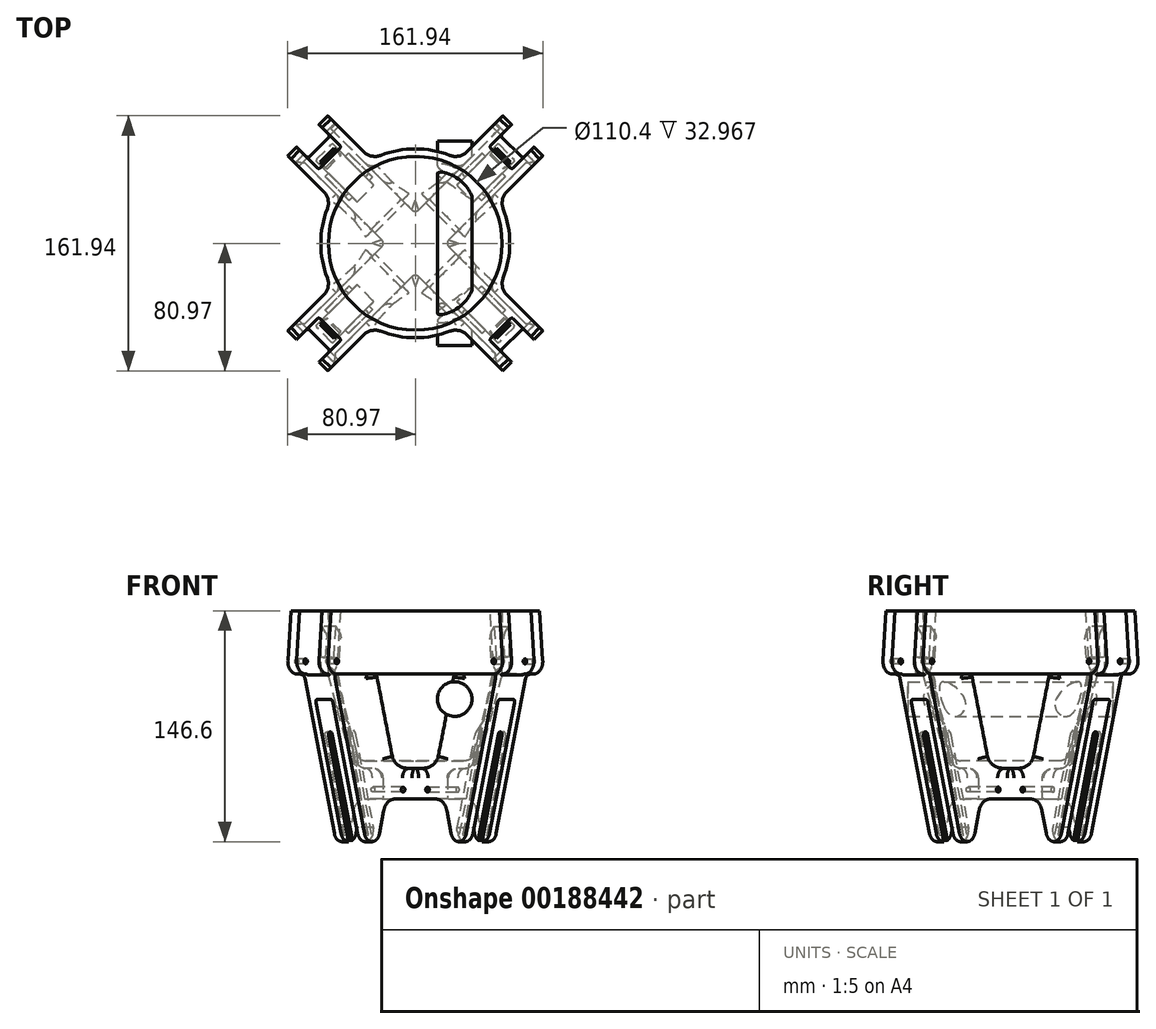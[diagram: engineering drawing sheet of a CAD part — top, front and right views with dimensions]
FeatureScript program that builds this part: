
annotation { "Feature Type Name" : "Feature", "Feature Type Description" : "" }
export const myFeature = defineFeature(function(context is Context, id is Id, definition is map)
    precondition{}
    {
        {
            var Q0;
            Q0=qCreatedBy(makeId("Top.planeOp"),FACE);
            var sketch = newSketch(context, id + "F0", { "sketchPlane" : qUnion([Q0])});
            skCircle(sketch, "E0", {"center": v(0, 0) * mm, "radius": 230 * mm, "construction": true});
            skLineSegment(sketch, "E1", {"start": v(-162.63, 162.63) * mm, "end": v(162.63, -162.63) * mm, "construction": true});
            skLineSegment(sketch, "E2", {"start": v(-162.63, -162.63) * mm, "end": v(162.63, 162.63) * mm, "construction": true});
            skLineSegment(sketch, "E3", {"start": v(0, 230) * mm, "end": v(0, -230) * mm, "construction": true});
            skCircle(sketch, "E4", {"center": v(-162.63, 162.63) * mm, "radius": 139.7 * mm, "construction": true});
            skCircle(sketch, "E5", {"center": v(162.63, 162.63) * mm, "radius": 139.7 * mm, "construction": true});
            skCircle(sketch, "E6", {"center": v(162.63, -162.63) * mm, "radius": 139.7 * mm, "construction": true});
            skCircle(sketch, "E7", {"center": v(-162.63, -162.63) * mm, "radius": 139.7 * mm, "construction": true});
            skCircle(sketch, "E8", {"center": v(0, 0) * mm, "radius": 80 * mm, "construction": true});
            skSolve(sketch);
        }
        {
            var Q0;
            Q0=sQuery(id+"F0.wireOp",EDGE,"E2");
            cPlane(context, id + "F1", {"entities" : qUnion([Q0]), "cplaneType" : CPlaneType.LINE_ANGLE, "offset" : 25 * mm, "angle" : 90 * degree, "width" : 150 * mm, "height" : 150 * mm});
        }
        {
            var Q0;
            Q0=qCreatedBy(id+"F1.planeOp",FACE);
            var sketch = newSketch(context, id + "F2", { "sketchPlane" : qUnion([Q0])});
            skLineSegment(sketch, "E9", {"start": v(0, 304.8) * mm, "end": v(0, -303.3) * mm, "construction": true});
            skLineSegment(sketch, "E10", {"start": v(0, 0) * mm, "end": v(244.07, 21.35) * mm, "construction": true});
            skLineSegment(sketch, "E11.0", {"start": v(80, 304.8) * mm, "end": v(80, -303.3) * mm, "construction": true});
            skLineSegment(sketch, "E12", {"start": v(244.07, 21.35) * mm, "end": v(243.52, 27.58) * mm});
            skLineSegment(sketch, "E13", {"start": v(243.52, 27.58) * mm, "end": v(74.17, 12.76) * mm});
            skLineSegment(sketch, "E14", {"start": v(74.17, 12.76) * mm, "end": v(74.71, 6.54) * mm});
            skLineSegment(sketch, "E15.MirrorCS", {"start": v(244.07, 21.35) * mm, "end": v(244.61, 15.13) * mm});
            skLineSegment(sketch, "E16.MirrorCS", {"start": v(75.26, 0.31) * mm, "end": v(74.71, 6.54) * mm});
            skLineSegment(sketch, "E17.MirrorCS", {"start": v(244.61, 15.13) * mm, "end": v(75.26, 0.31) * mm});
            skLineSegment(sketch, "E18", {"start": v(77.78, 28.89) * mm, "end": v(80.55, -2.74) * mm});
            skLineSegment(sketch, "E19", {"start": v(77.78, 28.89) * mm, "end": v(89.73, 29.93) * mm});
            skLineSegment(sketch, "E20", {"start": v(89.73, 29.93) * mm, "end": v(93.9, 18.5) * mm});
            skLineSegment(sketch, "E21", {"start": v(93.9, 18.5) * mm, "end": v(128.61, 21.54) * mm});
            skLineSegment(sketch, "E22", {"start": v(128.61, 21.54) * mm, "end": v(130.36, 1.62) * mm});
            skLineSegment(sketch, "E23", {"start": v(130.36, 1.62) * mm, "end": v(96.48, -1.35) * mm});
            skArc(sketch, "E24", {"start": v(80.55, -2.74) * mm, "mid": v(89.21, -10.01) * mm, "end": v(96.48, -1.35) * mm});
            skCircle(sketch, "E25", {"center": v(122.53, 10.72) * mm, "radius": 1.59 * mm});
            skLineSegment(sketch, "E26", {"start": v(88.51, -2.04) * mm, "end": v(87.67, 7.67) * mm, "construction": true});
            skLineSegment(sketch, "E27", {"start": v(88.51, -2.04) * mm, "end": v(88.51, -82.67) * mm, "construction": true});
            skCircle(sketch, "E28", {"center": v(88.51, -2.04) * mm, "radius": 157.3 * mm, "construction": true});
            skLineSegment(sketch, "E29", {"start": v(88.51, -2.04) * mm, "end": v(47.8, -153.99) * mm, "construction": true});
            skLineSegment(sketch, "E30.0", {"start": v(81.75, -0.23) * mm, "end": v(42.92, -145.15) * mm, "construction": true});
            skCircle(sketch, "E31", {"center": v(88.51, -2.04) * mm, "radius": 36.33 * mm, "construction": true});
            skLineSegment(sketch, "E32.0", {"start": v(98.01, -4.27) * mm, "end": v(57.3, -156.22) * mm, "construction": true});
            skPoint(sketch, "E33", {"position": v(88.87, -38.37) * mm});
            skCircle(sketch, "E34", {"center": v(88.87, -38.37) * mm, "radius": 1.59 * mm});
            skCircle(sketch, "E35", {"center": v(122.53, 10.72) * mm, "radius": 80 * mm, "construction": true});
            skLineSegment(sketch, "E36", {"start": v(122.53, 10.72) * mm, "end": v(68.8, -48.55) * mm, "construction": true});
            skArc(sketch, "E37.0.startCap", {"start": v(118.83, 14.08) * mm, "mid": v(125.89, 14.42) * mm, "end": v(126.24, 7.36) * mm});
            skArc(sketch, "E37.0.endCap", {"start": v(72.51, -51.91) * mm, "mid": v(65.45, -52.26) * mm, "end": v(65.1, -45.2) * mm});
            skLineSegment(sketch, "E37.0.left", {"start": v(126.24, 7.36) * mm, "end": v(72.51, -51.91) * mm});
            skLineSegment(sketch, "E37.0.right", {"start": v(118.83, 14.08) * mm, "end": v(65.1, -45.2) * mm});
            skCircle(sketch, "E38", {"center": v(88.51, -2.04) * mm, "radius": 1.59 * mm});
            skCircle(sketch, "E39", {"center": v(68.8, -48.55) * mm, "radius": 1.59 * mm});
            skCircle(sketch, "E40", {"center": v(88.87, -38.37) * mm, "radius": 80 * mm, "construction": true});
            skPoint(sketch, "E41", {"position": v(52.45, -109.6) * mm});
            skLineSegment(sketch, "E42", {"start": v(68.8, -48.55) * mm, "end": v(139.52, -119.26) * mm, "construction": true});
            skLineSegment(sketch, "E43", {"start": v(148.5, -119.26) * mm, "end": v(130.54, -119.26) * mm});
            skLineSegment(sketch, "E44", {"start": v(130.54, -119.26) * mm, "end": v(59.83, -48.55) * mm});
            skLineSegment(sketch, "E45", {"start": v(59.83, -48.55) * mm, "end": v(68.8, -39.57) * mm});
            skLineSegment(sketch, "E46", {"start": v(68.8, -39.57) * mm, "end": v(148.5, -119.26) * mm});
            skCircle(sketch, "E47", {"center": v(68.8, -48.55) * mm, "radius": 100 * mm, "construction": true});
            skCircle(sketch, "E48", {"center": v(122.69, -102.44) * mm, "radius": 1.59 * mm});
            skCircle(sketch, "E49", {"center": v(52.45, -109.6) * mm, "radius": 1.59 * mm});
            skLineSegment(sketch, "E50", {"start": v(52.45, -109.6) * mm, "end": v(26.57, -206.2) * mm, "construction": true});
            skLineSegment(sketch, "E51", {"start": v(22.08, -198.42) * mm, "end": v(47.96, -101.82) * mm});
            skLineSegment(sketch, "E52", {"start": v(47.96, -101.82) * mm, "end": v(60.23, -105.11) * mm});
            skCircle(sketch, "E53", {"center": v(32.73, -183.2) * mm, "radius": 1.59 * mm});
            skLineSegment(sketch, "E54", {"start": v(60.23, -105.11) * mm, "end": v(31.06, -213.97) * mm});
            skLineSegment(sketch, "E55", {"start": v(31.06, -213.97) * mm, "end": v(22.08, -198.42) * mm});
            skLineSegment(sketch, "E56", {"start": v(88.87, -38.37) * mm, "end": v(52.45, -109.6) * mm, "construction": true});
            skCircle(sketch, "E57", {"center": v(122.69, -102.44) * mm, "radius": 100 * mm, "construction": true});
            skCircle(sketch, "E58", {"center": v(32.73, -183.2) * mm, "radius": 100 * mm, "construction": true});
            skCircle(sketch, "E59", {"center": v(24.49, -83.54) * mm, "radius": 1.59 * mm});
            skLineSegment(sketch, "E60", {"start": v(24.49, -83.54) * mm, "end": v(122.69, -102.44) * mm, "construction": true});
            skArc(sketch, "E61.0.startCap", {"start": v(23.54, -88.45) * mm, "mid": v(19.58, -82.6) * mm, "end": v(25.43, -78.63) * mm});
            skArc(sketch, "E61.0.endCap", {"start": v(123.63, -97.53) * mm, "mid": v(127.6, -103.38) * mm, "end": v(121.74, -107.35) * mm});
            skLineSegment(sketch, "E61.0.left", {"start": v(25.43, -78.63) * mm, "end": v(123.63, -97.53) * mm});
            skLineSegment(sketch, "E61.0.right", {"start": v(23.54, -88.45) * mm, "end": v(121.74, -107.35) * mm});
            skLineSegment(sketch, "E62", {"start": v(24.49, -83.54) * mm, "end": v(32.73, -183.2) * mm, "construction": true});
            skArc(sketch, "E63.0.startCap", {"start": v(19.5, -83.96) * mm, "mid": v(24.08, -78.56) * mm, "end": v(29.47, -83.13) * mm});
            skArc(sketch, "E63.0.endCap", {"start": v(37.7, -182.8) * mm, "mid": v(33.14, -188.19) * mm, "end": v(27.74, -183.62) * mm});
            skLineSegment(sketch, "E63.0.left", {"start": v(29.47, -83.13) * mm, "end": v(37.7, -182.8) * mm});
            skLineSegment(sketch, "E63.0.right", {"start": v(19.5, -83.96) * mm, "end": v(27.74, -183.62) * mm});
            skCircle(sketch, "E64", {"center": v(88.51, -2.04) * mm, "radius": 32.74 * mm, "construction": true});
            skLineSegment(sketch, "E65", {"start": v(88.51, -2.04) * mm, "end": v(121.26, -2.04) * mm, "construction": true});
            skLineSegment(sketch, "E66.0", {"start": v(354.77, 67.43) * mm, "end": v(76.44, 43.08) * mm});
            skLineSegment(sketch, "E67", {"start": v(218.22, 25.37) * mm, "end": v(215.6, 55.25) * mm, "construction": true});
            skCircle(sketch, "E68", {"center": v(88.51, -2.04) * mm, "radius": 275.17 * mm, "construction": true});
            skLineSegment(sketch, "E69.0", {"start": v(135.04, -6.12) * mm, "end": v(62.73, -276) * mm});
            skLineSegment(sketch, "E70", {"start": v(89.73, 29.93) * mm, "end": v(0, 29.93) * mm, "construction": true});
            skSolve(sketch);
        }
        {
            var Q0;
            Q0=qCreatedBy(id+"F1.planeOp",FACE);
            var sketch = newSketch(context, id + "F3", { "sketchPlane" : qUnion([Q0])});
            skLineSegment(sketch, "E71", {"start": v(96.48, -1.35) * mm, "end": v(93.74, 30) * mm});
            skLineSegment(sketch, "E72", {"start": v(93.74, 30) * mm, "end": v(0, 30) * mm});
            skLineSegment(sketch, "E73", {"start": v(0, 30) * mm, "end": v(0, -89.54) * mm});
            skLineSegment(sketch, "E74", {"start": v(0, -89.54) * mm, "end": v(32.15, -89.54) * mm});
            skLineSegment(sketch, "E75", {"start": v(41.81, -96.96) * mm, "end": v(45.69, -111.41) * mm});
            skLineSegment(sketch, "E76", {"start": v(59.2, -111.41) * mm, "end": v(85.78, -12.27) * mm});
            skArc(sketch, "E77", {"start": v(88.63, -10.04) * mm, "mid": v(94.45, -7.4) * mm, "end": v(96.48, -1.35) * mm});
            skArc(sketch, "E78.filletArc", {"start": v(45.69, -111.41) * mm, "mid": v(52.45, -116.6) * mm, "end": v(59.2, -111.41) * mm});
            skPoint(sketch, "E79.visualSharp", {"position": v(39.83, -89.54) * mm});
            skArc(sketch, "E79.filletArc", {"start": v(41.81, -96.96) * mm, "mid": v(38.24, -91.61) * mm, "end": v(32.15, -89.54) * mm});
            skPoint(sketch, "E80.visualSharp", {"position": v(86.44, -9.77) * mm});
            skArc(sketch, "E80.filletArc", {"start": v(88.63, -10.04) * mm, "mid": v(86.83, -10.68) * mm, "end": v(85.78, -12.27) * mm});
            skPoint(sketch, "E81", {"position": v(24.49, -83.54) * mm});
            skSolve(sketch);
        }
        {
            var Q0;
            Q0 = qSketchRegion(id + "F3", true);
            extrude(context, id + "F4", {"entities" : qUnion([Q0]), "endBound" : BoundingType.SYMMETRIC, "depth" : 36 * mm, "offsetDistance" : 25 * mm});
        }
        {
            var Q0;
            Q0=qCreatedBy(id+"F1.planeOp",FACE);
            var sketch = newSketch(context, id + "F5", { "sketchPlane" : qUnion([Q0])});
            skLineSegment(sketch, "E82", {"start": v(76.68, 30) * mm, "end": v(79.55, -2.83) * mm});
            skLineSegment(sketch, "E83", {"start": v(76.68, 30) * mm, "end": v(94.75, 30) * mm});
            skLineSegment(sketch, "E84", {"start": v(94.75, 30) * mm, "end": v(98.34, -11.04) * mm});
            skLineSegment(sketch, "E85", {"start": v(98.34, -11.04) * mm, "end": v(88.51, -11.04) * mm});
            skArc(sketch, "E86", {"start": v(79.55, -2.83) * mm, "mid": v(82.43, -8.68) * mm, "end": v(88.51, -11.04) * mm});
            skSolve(sketch);
        }
        {
            var Q0;
            Q0 = qSketchRegion(id + "F5", true);
            extrude(context, id + "F6", {"entities" : qUnion([Q0]), "operationType" : NewBodyOperationType.REMOVE, "endBound" : BoundingType.SYMMETRIC, "oppositeDirection" : true, "depth" : 20 * mm, "offsetDistance" : 25 * mm});
        }
        {
            var Q0;
            Q0=makeQuery(id+"F4.opExtrude","SWEPT_FACE",FACE,{"disambiguationData":[OSD([sQuery(id+"F3.wireOp",EDGE,"E73")])]});
            var sketch = newSketch(context, id + "F7", { "sketchPlane" : qUnion([Q0])});
            skLineSegment(sketch, "E87", {"start": v(13.5, -119.35) * mm, "end": v(13.5, -10) * mm});
            skLineSegment(sketch, "E88", {"start": v(18, -10) * mm, "end": v(18, -125.35) * mm});
            skLineSegment(sketch, "E89", {"start": v(18, -125.35) * mm, "end": v(0, -125.35) * mm});
            skLineSegment(sketch, "E90", {"start": v(13.5, -119.35) * mm, "end": v(0, -119.35) * mm});
            skLineSegment(sketch, "E91", {"start": v(0, -131.37) * mm, "end": v(0, 49.73) * mm, "construction": true});
            skLineSegment(sketch, "E92.MirrorCS", {"start": v(-13.5, -119.35) * mm, "end": v(0, -119.35) * mm});
            skLineSegment(sketch, "E93.MirrorCS", {"start": v(-18, -125.35) * mm, "end": v(0, -125.35) * mm});
            skLineSegment(sketch, "E94.MirrorCS", {"start": v(-13.5, -119.35) * mm, "end": v(-13.5, -10) * mm});
            skLineSegment(sketch, "E95.MirrorCS", {"start": v(-18, -10) * mm, "end": v(-18, -125.35) * mm});
            skLineSegment(sketch, "E96", {"start": v(18, -10) * mm, "end": v(13.5, -10) * mm});
            skLineSegment(sketch, "E97", {"start": v(-18, -10) * mm, "end": v(-13.5, -10) * mm});
            skSolve(sketch);
        }
        {
            var Q0;
            Q0 = qSketchRegion(id + "F7", true);
            extrude(context, id + "F8", {"entities" : qUnion([Q0]), "operationType" : NewBodyOperationType.REMOVE, "oppositeDirection" : true, "depth" : 100 * mm, "offsetDistance" : 25 * mm});
        }
        {
            var Q0;
            Q0=makeQuery(id+"F4.opExtrude","CAP_FACE",FACE,{"disambiguationData":[OSD([sQuery(id+"F3.wireOp",EDGE,"E71"),sQuery(id+"F3.wireOp",EDGE,"E72"),sQuery(id+"F3.wireOp",EDGE,"E73"),sQuery(id+"F3.wireOp",EDGE,"E74"),sQuery(id+"F3.wireOp",EDGE,"E75"),sQuery(id+"F3.wireOp",EDGE,"E76"),sQuery(id+"F3.wireOp",EDGE,"E77"),sQuery(id+"F3.wireOp",EDGE,"E78.filletArc"),sQuery(id+"F3.wireOp",EDGE,"E79.filletArc"),sQuery(id+"F3.wireOp",EDGE,"E80.filletArc")])],"isStart":false});
            var sketch = newSketch(context, id + "F9", { "sketchPlane" : qUnion([Q0])});
            skCircle(sketch, "E98", {"center": v(88.51, -2.04) * mm, "radius": 1.59 * mm});
            skSolve(sketch);
        }
        {
            var Q0;
            Q0 = qSketchRegion(id + "F9", true);
            var Q1;
            Q1=makeQuery(id+"F4.opExtrude","CAP_FACE",FACE,{"disambiguationData":[OSD([sQuery(id+"F3.wireOp",EDGE,"E71"),sQuery(id+"F3.wireOp",EDGE,"E72"),sQuery(id+"F3.wireOp",EDGE,"E73"),sQuery(id+"F3.wireOp",EDGE,"E74"),sQuery(id+"F3.wireOp",EDGE,"E75"),sQuery(id+"F3.wireOp",EDGE,"E76"),sQuery(id+"F3.wireOp",EDGE,"E77"),sQuery(id+"F3.wireOp",EDGE,"E78.filletArc"),sQuery(id+"F3.wireOp",EDGE,"E79.filletArc"),sQuery(id+"F3.wireOp",EDGE,"E80.filletArc")])],"isStart":true});
            extrude(context, id + "F10", {"entities" : qUnion([Q0]), "operationType" : NewBodyOperationType.REMOVE, "endBound" : BoundingType.UP_TO_SURFACE, "oppositeDirection" : true, "depth" : 25 * mm, "endBoundEntityFace" : qUnion([Q1]), "offsetDistance" : 25 * mm});
        }
        {
            var Q0;
            Q0=makeQuery(id+"F8.boolean.opBoolean","COPY",FACE,{"derivedFrom":makeQuery(id+"F8.opExtrude","SWEPT_FACE",FACE,{"disambiguationData":[OSD([sQuery(id+"F7.wireOp",EDGE,"E87")])]})});
            var sketch = newSketch(context, id + "F11", { "sketchPlane" : qUnion([Q0])});
            skCircle(sketch, "E99", {"center": v(24.49, -83.54) * mm, "radius": 1.59 * mm});
            skSolve(sketch);
        }
        {
            var Q0;
            Q0 = qSketchRegion(id + "F11", true);
            var Q1;
            Q1=makeQuery(id+"F8.boolean.opBoolean","COPY",FACE,{"derivedFrom":makeQuery(id+"F8.opExtrude","SWEPT_FACE",FACE,{"disambiguationData":[OSD([sQuery(id+"F7.wireOp",EDGE,"E94.MirrorCS")])]})});
            extrude(context, id + "F12", {"entities" : qUnion([Q0]), "operationType" : NewBodyOperationType.REMOVE, "endBound" : BoundingType.UP_TO_SURFACE, "oppositeDirection" : true, "depth" : 25 * mm, "endBoundEntityFace" : qUnion([Q1]), "offsetDistance" : 25 * mm});
        }
        {
            var Q0;
            Q0=qCreatedBy(id+"F1.planeOp",FACE);
            var sketch = newSketch(context, id + "F13", { "sketchPlane" : qUnion([Q0])});
            skLineSegment(sketch, "E100", {"start": v(61.73, -46.65) * mm, "end": v(82, -26.39) * mm});
            skLineSegment(sketch, "E101", {"start": v(60.43, -48.9) * mm, "end": v(42.9, -114.3) * mm});
            skLineSegment(sketch, "E102", {"start": v(42.9, -114.3) * mm, "end": v(57.4, -118.17) * mm});
            skLineSegment(sketch, "E103", {"start": v(57.4, -118.17) * mm, "end": v(82, -26.39) * mm});
            skPoint(sketch, "E104.visualSharp", {"position": v(60.78, -47.6) * mm});
            skArc(sketch, "E104.filletArc", {"start": v(61.73, -46.65) * mm, "mid": v(60.93, -47.69) * mm, "end": v(60.43, -48.9) * mm});
            skSolve(sketch);
        }
        {
            var Q0;
            Q0 = qSketchRegion(id + "F13", true);
            extrude(context, id + "F14", {"entities" : qUnion([Q0]), "operationType" : NewBodyOperationType.REMOVE, "endBound" : BoundingType.SYMMETRIC, "oppositeDirection" : true, "depth" : 15 * mm, "offsetDistance" : 25 * mm});
        }
        {
            var Q0;
            Q0=qCreatedBy(id+"F1.planeOp",FACE);
            var sketch = newSketch(context, id + "F15", { "sketchPlane" : qUnion([Q0])});
            skLineSegment(sketch, "E105", {"start": v(68.8, -48.55) * mm, "end": v(50.64, -116.36) * mm, "construction": true});
            skArc(sketch, "E106.0.startCap", {"start": v(67.11, -48.1) * mm, "mid": v(69.26, -46.86) * mm, "end": v(70.5, -49) * mm});
            skArc(sketch, "E106.0.endCap", {"start": v(52.33, -116.81) * mm, "mid": v(50.18, -118.05) * mm, "end": v(48.95, -115.9) * mm});
            skLineSegment(sketch, "E106.0.left", {"start": v(70.5, -49) * mm, "end": v(52.33, -116.81) * mm});
            skLineSegment(sketch, "E106.0.right", {"start": v(67.11, -48.1) * mm, "end": v(48.95, -115.9) * mm});
            skSolve(sketch);
        }
        {
            var Q0;
            Q0 = qSketchRegion(id + "F15", true);
            extrude(context, id + "F16", {"entities" : qUnion([Q0]), "operationType" : NewBodyOperationType.REMOVE, "endBound" : BoundingType.SYMMETRIC, "oppositeDirection" : true, "depth" : 21 * mm, "offsetDistance" : 25 * mm});
        }
        {
            var Q0;
            Q0=qCreatedBy(id+"F1.planeOp",FACE);
            var sketch = newSketch(context, id + "F17", { "sketchPlane" : qUnion([Q0])});
            skLineSegment(sketch, "E107", {"start": v(80.24, 0.75) * mm, "end": v(74.26, 0.22) * mm});
            skLineSegment(sketch, "E108", {"start": v(74.26, 0.22) * mm, "end": v(73.17, 12.68) * mm});
            skLineSegment(sketch, "E109", {"start": v(74.32, 16.33) * mm, "end": v(78.45, 21.24) * mm});
            skLineSegment(sketch, "E110", {"start": v(78.45, 21.24) * mm, "end": v(80.24, 0.75) * mm});
            skCircle(sketch, "E111", {"center": v(88.51, -2.04) * mm, "radius": 13.46 * mm, "construction": true});
            skPoint(sketch, "E112.visualSharp", {"position": v(73, 14.74) * mm});
            skArc(sketch, "E112.filletArc", {"start": v(74.32, 16.33) * mm, "mid": v(73.39, 14.62) * mm, "end": v(73.17, 12.68) * mm});
            skSolve(sketch);
        }
        {
            var Q0;
            Q0 = qSketchRegion(id + "F17", true);
            extrude(context, id + "F18", {"entities" : qUnion([Q0]), "operationType" : NewBodyOperationType.REMOVE, "endBound" : BoundingType.SYMMETRIC, "oppositeDirection" : true, "depth" : 12.5 * mm, "offsetDistance" : 25 * mm});
        }
        {
            var Q0;
            Q0=makeQuery(id+"F4.opExtrude","SWEPT_BODY",BODY,{"disambiguationData":[OSD([sQuery(id+"F3.wireOp",EDGE,"E71"),sQuery(id+"F3.wireOp",EDGE,"E72"),sQuery(id+"F3.wireOp",EDGE,"E73"),sQuery(id+"F3.wireOp",EDGE,"E74"),sQuery(id+"F3.wireOp",EDGE,"E75"),sQuery(id+"F3.wireOp",EDGE,"E76"),sQuery(id+"F3.wireOp",EDGE,"E77"),sQuery(id+"F3.wireOp",EDGE,"E78.filletArc"),sQuery(id+"F3.wireOp",EDGE,"E79.filletArc"),sQuery(id+"F3.wireOp",EDGE,"E80.filletArc")])]});
            var Q1;
            Q1=sQuery(id+"F2.wireOp",EDGE,"E9");
            circularPattern(context, id + "F19", {"operationType" : NewBodyOperationType.ADD, "entities" : qUnion([Q0]), "axis" : qUnion([Q1]), "angle" : 360 * degree, "instanceCount" : 4, "equalSpace" : true});
        }
        {
            var Q0;
            Q0=qCreatedBy(id+"F1.planeOp",FACE);
            var sketch = newSketch(context, id + "F20", { "sketchPlane" : qUnion([Q0])});
            skLineSegment(sketch, "E113", {"start": v(0, 36.38) * mm, "end": v(0, -126.2) * mm, "construction": true});
            skLineSegment(sketch, "E114", {"start": v(0, 30) * mm, "end": v(60, 30) * mm});
            skLineSegment(sketch, "E115", {"start": v(60, 30) * mm, "end": v(60, -10) * mm});
            skLineSegment(sketch, "E116", {"start": v(55.5, -10) * mm, "end": v(41.4, -62.59) * mm});
            skLineSegment(sketch, "E117", {"start": v(31.75, -70) * mm, "end": v(0, -70) * mm});
            skLineSegment(sketch, "E118", {"start": v(0, -70) * mm, "end": v(0, 30) * mm});
            skPoint(sketch, "E119.visualSharp", {"position": v(39.42, -70) * mm});
            skArc(sketch, "E119.filletArc", {"start": v(31.75, -70) * mm, "mid": v(37.84, -67.93) * mm, "end": v(41.4, -62.59) * mm});
            skLineSegment(sketch, "E120", {"start": v(55.5, -10) * mm, "end": v(60, -10) * mm});
            skSolve(sketch);
        }
        {
            var Q0;
            Q0 = qSketchRegion(id + "F20", true);
            var Q1;
            Q1=sQuery(id+"F20.wireOp",EDGE,"E113");
            revolve(context, id + "F21", {"operationType" : NewBodyOperationType.ADD, "surfaceOperationType" : NewSurfaceOperationType.NEW, "entities" : qUnion([Q0]), "axis" : qUnion([Q1]), "revolveType" : RevolveType.FULL});
        }
        {
            var Q0;
            Q0=makeQuery(id+"F21.boolean.opBoolean","INTERSECT",EDGE,{"derivedFrom":[makeQuery(id+"F19.opPattern","COPY",FACE,{"derivedFrom":makeQuery(id+"F4.opExtrude","CAP_FACE",FACE,{"disambiguationData":[OSD([sQuery(id+"F3.wireOp",EDGE,"E71"),sQuery(id+"F3.wireOp",EDGE,"E72"),sQuery(id+"F3.wireOp",EDGE,"E73"),sQuery(id+"F3.wireOp",EDGE,"E74"),sQuery(id+"F3.wireOp",EDGE,"E75"),sQuery(id+"F3.wireOp",EDGE,"E76"),sQuery(id+"F3.wireOp",EDGE,"E77"),sQuery(id+"F3.wireOp",EDGE,"E78.filletArc"),sQuery(id+"F3.wireOp",EDGE,"E79.filletArc"),sQuery(id+"F3.wireOp",EDGE,"E80.filletArc")])],"isStart":true}),"instanceName":"3"}),makeQuery(id+"F21.opRevolve","SWEPT_FACE",FACE,{"disambiguationData":[OSD([sQuery(id+"F20.wireOp",EDGE,"E115")])]})]});
            var Q1;
            Q1=makeQuery(id+"F21.boolean.opBoolean","INTERSECT",EDGE,{"derivedFrom":[makeQuery(id+"F19.opPattern","COPY",FACE,{"derivedFrom":makeQuery(id+"F4.opExtrude","CAP_FACE",FACE,{"disambiguationData":[OSD([sQuery(id+"F3.wireOp",EDGE,"E71"),sQuery(id+"F3.wireOp",EDGE,"E72"),sQuery(id+"F3.wireOp",EDGE,"E73"),sQuery(id+"F3.wireOp",EDGE,"E74"),sQuery(id+"F3.wireOp",EDGE,"E75"),sQuery(id+"F3.wireOp",EDGE,"E76"),sQuery(id+"F3.wireOp",EDGE,"E77"),sQuery(id+"F3.wireOp",EDGE,"E78.filletArc"),sQuery(id+"F3.wireOp",EDGE,"E79.filletArc"),sQuery(id+"F3.wireOp",EDGE,"E80.filletArc")])],"isStart":false}),"instanceName":"2"}),makeQuery(id+"F21.opRevolve","SWEPT_FACE",FACE,{"disambiguationData":[OSD([sQuery(id+"F20.wireOp",EDGE,"E115")])]})]});
            var Q2;
            Q2=makeQuery(id+"F21.boolean.opBoolean","INTERSECT",EDGE,{"derivedFrom":[makeQuery(id+"F19.opPattern","COPY",FACE,{"derivedFrom":makeQuery(id+"F4.opExtrude","CAP_FACE",FACE,{"disambiguationData":[OSD([sQuery(id+"F3.wireOp",EDGE,"E71"),sQuery(id+"F3.wireOp",EDGE,"E72"),sQuery(id+"F3.wireOp",EDGE,"E73"),sQuery(id+"F3.wireOp",EDGE,"E74"),sQuery(id+"F3.wireOp",EDGE,"E75"),sQuery(id+"F3.wireOp",EDGE,"E76"),sQuery(id+"F3.wireOp",EDGE,"E77"),sQuery(id+"F3.wireOp",EDGE,"E78.filletArc"),sQuery(id+"F3.wireOp",EDGE,"E79.filletArc"),sQuery(id+"F3.wireOp",EDGE,"E80.filletArc")])],"isStart":true}),"instanceName":"2"}),makeQuery(id+"F21.opRevolve","SWEPT_FACE",FACE,{"disambiguationData":[OSD([sQuery(id+"F20.wireOp",EDGE,"E115")])]})]});
            var Q3;
            Q3=makeQuery(id+"F21.boolean.opBoolean","INTERSECT",EDGE,{"derivedFrom":[makeQuery(id+"F19.opPattern","COPY",FACE,{"derivedFrom":makeQuery(id+"F4.opExtrude","CAP_FACE",FACE,{"disambiguationData":[OSD([sQuery(id+"F3.wireOp",EDGE,"E71"),sQuery(id+"F3.wireOp",EDGE,"E72"),sQuery(id+"F3.wireOp",EDGE,"E73"),sQuery(id+"F3.wireOp",EDGE,"E74"),sQuery(id+"F3.wireOp",EDGE,"E75"),sQuery(id+"F3.wireOp",EDGE,"E76"),sQuery(id+"F3.wireOp",EDGE,"E77"),sQuery(id+"F3.wireOp",EDGE,"E78.filletArc"),sQuery(id+"F3.wireOp",EDGE,"E79.filletArc"),sQuery(id+"F3.wireOp",EDGE,"E80.filletArc")])],"isStart":false}),"instanceName":"1"}),makeQuery(id+"F21.opRevolve","SWEPT_FACE",FACE,{"disambiguationData":[OSD([sQuery(id+"F20.wireOp",EDGE,"E115")])]})]});
            var Q4;
            {var subQ0=sQuery(id+"F3.wireOp",EDGE,"E80.filletArc");var subQ1=sQuery(id+"F3.wireOp",EDGE,"E79.filletArc");var subQ2=sQuery(id+"F3.wireOp",EDGE,"E78.filletArc");var subQ3=sQuery(id+"F3.wireOp",EDGE,"E77");var subQ4=sQuery(id+"F3.wireOp",EDGE,"E76");var subQ5=sQuery(id+"F3.wireOp",EDGE,"E75");var subQ6=sQuery(id+"F3.wireOp",EDGE,"E74");var subQ7=sQuery(id+"F3.wireOp",EDGE,"E73");var subQ8=sQuery(id+"F3.wireOp",EDGE,"E72");var subQ9=sQuery(id+"F3.wireOp",EDGE,"E71");Q4=makeQuery(id+"F21.boolean.opBoolean","INTERSECT",EDGE,{"derivedFrom":[makeQuery(id+"F19.boolean.opBoolean","MERGE",FACE,{"disambiguationData":[OD(0.0)],"derivedFrom":[makeQuery(id+"F19.opPattern","COPY",FACE,{"derivedFrom":makeQuery(id+"F4.opExtrude","CAP_FACE",FACE,{"disambiguationData":[OSD([subQ9,subQ8,subQ7,subQ6,subQ5,subQ4,subQ3,subQ2,subQ1,subQ0])],"isStart":true}),"instanceName":"1"}),makeQuery(id+"F19.opPattern","COPY",FACE,{"derivedFrom":makeQuery(id+"F4.opExtrude","CAP_FACE",FACE,{"disambiguationData":[OSD([subQ9,subQ8,subQ7,subQ6,subQ5,subQ4,subQ3,subQ2,subQ1,subQ0])],"isStart":false}),"instanceName":"3"})]}),makeQuery(id+"F21.opRevolve","SWEPT_FACE",FACE,{"disambiguationData":[OSD([sQuery(id+"F20.wireOp",EDGE,"E115")])]})]});}
            var Q5;
            Q5=makeQuery(id+"F21.boolean.opBoolean","INTERSECT",EDGE,{"derivedFrom":[makeQuery(id+"F4.opExtrude","CAP_FACE",FACE,{"disambiguationData":[OSD([sQuery(id+"F3.wireOp",EDGE,"E71"),sQuery(id+"F3.wireOp",EDGE,"E72"),sQuery(id+"F3.wireOp",EDGE,"E73"),sQuery(id+"F3.wireOp",EDGE,"E74"),sQuery(id+"F3.wireOp",EDGE,"E75"),sQuery(id+"F3.wireOp",EDGE,"E76"),sQuery(id+"F3.wireOp",EDGE,"E77"),sQuery(id+"F3.wireOp",EDGE,"E78.filletArc"),sQuery(id+"F3.wireOp",EDGE,"E79.filletArc"),sQuery(id+"F3.wireOp",EDGE,"E80.filletArc")])],"isStart":false}),makeQuery(id+"F21.opRevolve","SWEPT_FACE",FACE,{"disambiguationData":[OSD([sQuery(id+"F20.wireOp",EDGE,"E115")])]})]});
            var Q6;
            Q6=makeQuery(id+"F21.boolean.opBoolean","INTERSECT",EDGE,{"derivedFrom":[makeQuery(id+"F4.opExtrude","CAP_FACE",FACE,{"disambiguationData":[OSD([sQuery(id+"F3.wireOp",EDGE,"E71"),sQuery(id+"F3.wireOp",EDGE,"E72"),sQuery(id+"F3.wireOp",EDGE,"E73"),sQuery(id+"F3.wireOp",EDGE,"E74"),sQuery(id+"F3.wireOp",EDGE,"E75"),sQuery(id+"F3.wireOp",EDGE,"E76"),sQuery(id+"F3.wireOp",EDGE,"E77"),sQuery(id+"F3.wireOp",EDGE,"E78.filletArc"),sQuery(id+"F3.wireOp",EDGE,"E79.filletArc"),sQuery(id+"F3.wireOp",EDGE,"E80.filletArc")])],"isStart":true}),makeQuery(id+"F21.opRevolve","SWEPT_FACE",FACE,{"disambiguationData":[OSD([sQuery(id+"F20.wireOp",EDGE,"E115")])]})]});
            var Q7;
            {var subQ0=sQuery(id+"F3.wireOp",EDGE,"E80.filletArc");var subQ1=sQuery(id+"F3.wireOp",EDGE,"E79.filletArc");var subQ2=sQuery(id+"F3.wireOp",EDGE,"E78.filletArc");var subQ3=sQuery(id+"F3.wireOp",EDGE,"E77");var subQ4=sQuery(id+"F3.wireOp",EDGE,"E76");var subQ5=sQuery(id+"F3.wireOp",EDGE,"E75");var subQ6=sQuery(id+"F3.wireOp",EDGE,"E74");var subQ7=sQuery(id+"F3.wireOp",EDGE,"E73");var subQ8=sQuery(id+"F3.wireOp",EDGE,"E72");var subQ9=sQuery(id+"F3.wireOp",EDGE,"E71");Q7=makeQuery(id+"F21.boolean.opBoolean","INTERSECT",EDGE,{"derivedFrom":[makeQuery(id+"F19.boolean.opBoolean","MERGE",FACE,{"disambiguationData":[OD(1.0)],"derivedFrom":[makeQuery(id+"F19.opPattern","COPY",FACE,{"derivedFrom":makeQuery(id+"F4.opExtrude","CAP_FACE",FACE,{"disambiguationData":[OSD([subQ9,subQ8,subQ7,subQ6,subQ5,subQ4,subQ3,subQ2,subQ1,subQ0])],"isStart":true}),"instanceName":"1"}),makeQuery(id+"F19.opPattern","COPY",FACE,{"derivedFrom":makeQuery(id+"F4.opExtrude","CAP_FACE",FACE,{"disambiguationData":[OSD([subQ9,subQ8,subQ7,subQ6,subQ5,subQ4,subQ3,subQ2,subQ1,subQ0])],"isStart":false}),"instanceName":"3"})]}),makeQuery(id+"F21.opRevolve","SWEPT_FACE",FACE,{"disambiguationData":[OSD([sQuery(id+"F20.wireOp",EDGE,"E115")])]})]});}
            fillet(context, id + "F22", {"entities" : qUnion([Q0, Q1, Q2, Q3, Q4, Q5, Q6, Q7]), "radius" : 10 * mm, "tangentPropagation" : true, "allowEdgeOverflow" : false});
        }
        {
            var Q0;
            Q0=makeQuery(id+"F19.boolean.opBoolean","INTERSECT",EDGE,{"derivedFrom":[makeQuery(id+"F19.opPattern","COPY",FACE,{"derivedFrom":makeQuery(id+"F8.boolean.opBoolean","COPY",FACE,{"derivedFrom":makeQuery(id+"F8.opExtrude","SWEPT_FACE",FACE,{"disambiguationData":[OSD([sQuery(id+"F7.wireOp",EDGE,"E87")])]})}),"instanceName":"1"}),makeQuery(id+"F19.opPattern","COPY",FACE,{"derivedFrom":makeQuery(id+"F8.boolean.opBoolean","COPY",FACE,{"derivedFrom":makeQuery(id+"F8.opExtrude","SWEPT_FACE",FACE,{"disambiguationData":[OSD([sQuery(id+"F7.wireOp",EDGE,"E94.MirrorCS")])]})}),"instanceName":"2"})]});
            var Q1;
            {var subQ0=makeQuery(id+"F8.boolean.opBoolean","COPY",FACE,{"derivedFrom":makeQuery(id+"F8.opExtrude","SWEPT_FACE",FACE,{"disambiguationData":[OSD([sQuery(id+"F7.wireOp",EDGE,"E87")])]})});Q1=makeQuery(id+"F19.boolean.opBoolean","INTERSECT",EDGE,{"derivedFrom":[subQ0,makeQuery(id+"F19.opPattern","COPY",FACE,{"derivedFrom":makeQuery(id+"F8.boolean.opBoolean","COPY",FACE,{"derivedFrom":makeQuery(id+"F8.opExtrude","SWEPT_FACE",FACE,{"disambiguationData":[OSD([sQuery(id+"F7.wireOp",EDGE,"E94.MirrorCS")])]})}),"instanceName":"1"}),makeQuery(id+"F19.opPattern","COPY",FACE,{"derivedFrom":subQ0,"instanceName":"3"})]});}
            var Q2;
            {var subQ0=makeQuery(id+"F8.boolean.opBoolean","COPY",FACE,{"derivedFrom":makeQuery(id+"F8.opExtrude","SWEPT_FACE",FACE,{"disambiguationData":[OSD([sQuery(id+"F7.wireOp",EDGE,"E94.MirrorCS")])]})});Q2=makeQuery(id+"F19.boolean.opBoolean","INTERSECT",EDGE,{"derivedFrom":[subQ0,makeQuery(id+"F19.opPattern","COPY",FACE,{"derivedFrom":subQ0,"instanceName":"1"}),makeQuery(id+"F19.opPattern","COPY",FACE,{"derivedFrom":makeQuery(id+"F8.boolean.opBoolean","COPY",FACE,{"derivedFrom":makeQuery(id+"F8.opExtrude","SWEPT_FACE",FACE,{"disambiguationData":[OSD([sQuery(id+"F7.wireOp",EDGE,"E87")])]})}),"instanceName":"3"})]});}
            var Q3;
            Q3=makeQuery(id+"F19.boolean.opBoolean","INTERSECT",EDGE,{"derivedFrom":[makeQuery(id+"F19.opPattern","COPY",FACE,{"derivedFrom":makeQuery(id+"F8.boolean.opBoolean","COPY",FACE,{"derivedFrom":makeQuery(id+"F8.opExtrude","SWEPT_FACE",FACE,{"disambiguationData":[OSD([sQuery(id+"F7.wireOp",EDGE,"E87")])]})}),"instanceName":"2"}),makeQuery(id+"F19.opPattern","COPY",FACE,{"derivedFrom":makeQuery(id+"F8.boolean.opBoolean","COPY",FACE,{"derivedFrom":makeQuery(id+"F8.opExtrude","SWEPT_FACE",FACE,{"disambiguationData":[OSD([sQuery(id+"F7.wireOp",EDGE,"E94.MirrorCS")])]})}),"instanceName":"3"})]});
            fillet(context, id + "F23", {"entities" : qUnion([Q0, Q1, Q2, Q3]), "radius" : 3 * mm, "tangentPropagation" : true, "allowEdgeOverflow" : false});
        }
        {
            var Q0;
            Q0=makeQuery(id+"F14.boolean.opBoolean","COPY",EDGE,{"derivedFrom":makeQuery(id+"F14.opExtrude","CAP_EDGE",EDGE,{"disambiguationData":[OSD([sQuery(id+"F13.wireOp",EDGE,"E101")])],"isStart":true})});
            var Q1;
            Q1=makeQuery(id+"F14.boolean.opBoolean","COPY",EDGE,{"derivedFrom":makeQuery(id+"F14.opExtrude","CAP_EDGE",EDGE,{"disambiguationData":[OSD([sQuery(id+"F13.wireOp",EDGE,"E101")])],"isStart":false})});
            var Q2;
            Q2=makeQuery(id+"F6.boolean.opBoolean","COPY",EDGE,{"derivedFrom":makeQuery(id+"F6.opExtrude","CAP_EDGE",EDGE,{"disambiguationData":[OSD([sQuery(id+"F5.wireOp",EDGE,"E82")])],"isStart":false})});
            var Q3;
            Q3=makeQuery(id+"F6.boolean.opBoolean","COPY",EDGE,{"derivedFrom":makeQuery(id+"F6.opExtrude","CAP_EDGE",EDGE,{"disambiguationData":[OSD([sQuery(id+"F5.wireOp",EDGE,"E82")])],"isStart":true})});
            var Q4;
            Q4=makeQuery(id+"F19.opPattern","COPY",EDGE,{"derivedFrom":makeQuery(id+"F14.boolean.opBoolean","COPY",EDGE,{"derivedFrom":makeQuery(id+"F14.opExtrude","CAP_EDGE",EDGE,{"disambiguationData":[OSD([sQuery(id+"F13.wireOp",EDGE,"E101")])],"isStart":true})}),"instanceName":"3"});
            var Q5;
            Q5=makeQuery(id+"F19.opPattern","COPY",EDGE,{"derivedFrom":makeQuery(id+"F14.boolean.opBoolean","COPY",EDGE,{"derivedFrom":makeQuery(id+"F14.opExtrude","CAP_EDGE",EDGE,{"disambiguationData":[OSD([sQuery(id+"F13.wireOp",EDGE,"E101")])],"isStart":false})}),"instanceName":"3"});
            var Q6;
            Q6=makeQuery(id+"F19.opPattern","COPY",EDGE,{"derivedFrom":makeQuery(id+"F6.boolean.opBoolean","COPY",EDGE,{"derivedFrom":makeQuery(id+"F6.opExtrude","CAP_EDGE",EDGE,{"disambiguationData":[OSD([sQuery(id+"F5.wireOp",EDGE,"E82")])],"isStart":true})}),"instanceName":"3"});
            var Q7;
            Q7=makeQuery(id+"F19.opPattern","COPY",EDGE,{"derivedFrom":makeQuery(id+"F6.boolean.opBoolean","COPY",EDGE,{"derivedFrom":makeQuery(id+"F6.opExtrude","CAP_EDGE",EDGE,{"disambiguationData":[OSD([sQuery(id+"F5.wireOp",EDGE,"E82")])],"isStart":false})}),"instanceName":"3"});
            var Q8;
            Q8=makeQuery(id+"F19.opPattern","COPY",EDGE,{"derivedFrom":makeQuery(id+"F14.boolean.opBoolean","COPY",EDGE,{"derivedFrom":makeQuery(id+"F14.opExtrude","CAP_EDGE",EDGE,{"disambiguationData":[OSD([sQuery(id+"F13.wireOp",EDGE,"E101")])],"isStart":true})}),"instanceName":"2"});
            var Q9;
            Q9=makeQuery(id+"F19.opPattern","COPY",EDGE,{"derivedFrom":makeQuery(id+"F14.boolean.opBoolean","COPY",EDGE,{"derivedFrom":makeQuery(id+"F14.opExtrude","CAP_EDGE",EDGE,{"disambiguationData":[OSD([sQuery(id+"F13.wireOp",EDGE,"E101")])],"isStart":false})}),"instanceName":"2"});
            var Q10;
            Q10=makeQuery(id+"F19.opPattern","COPY",EDGE,{"derivedFrom":makeQuery(id+"F6.boolean.opBoolean","COPY",EDGE,{"derivedFrom":makeQuery(id+"F6.opExtrude","CAP_EDGE",EDGE,{"disambiguationData":[OSD([sQuery(id+"F5.wireOp",EDGE,"E82")])],"isStart":true})}),"instanceName":"2"});
            var Q11;
            Q11=makeQuery(id+"F19.opPattern","COPY",EDGE,{"derivedFrom":makeQuery(id+"F6.boolean.opBoolean","COPY",EDGE,{"derivedFrom":makeQuery(id+"F6.opExtrude","CAP_EDGE",EDGE,{"disambiguationData":[OSD([sQuery(id+"F5.wireOp",EDGE,"E82")])],"isStart":false})}),"instanceName":"2"});
            var Q12;
            Q12=makeQuery(id+"F19.opPattern","COPY",EDGE,{"derivedFrom":makeQuery(id+"F14.boolean.opBoolean","COPY",EDGE,{"derivedFrom":makeQuery(id+"F14.opExtrude","CAP_EDGE",EDGE,{"disambiguationData":[OSD([sQuery(id+"F13.wireOp",EDGE,"E101")])],"isStart":true})}),"instanceName":"1"});
            var Q13;
            Q13=makeQuery(id+"F19.opPattern","COPY",EDGE,{"derivedFrom":makeQuery(id+"F14.boolean.opBoolean","COPY",EDGE,{"derivedFrom":makeQuery(id+"F14.opExtrude","CAP_EDGE",EDGE,{"disambiguationData":[OSD([sQuery(id+"F13.wireOp",EDGE,"E101")])],"isStart":false})}),"instanceName":"1"});
            var Q14;
            Q14=makeQuery(id+"F19.opPattern","COPY",EDGE,{"derivedFrom":makeQuery(id+"F6.boolean.opBoolean","COPY",EDGE,{"derivedFrom":makeQuery(id+"F6.opExtrude","CAP_EDGE",EDGE,{"disambiguationData":[OSD([sQuery(id+"F5.wireOp",EDGE,"E82")])],"isStart":true})}),"instanceName":"1"});
            var Q15;
            Q15=makeQuery(id+"F19.opPattern","COPY",EDGE,{"derivedFrom":makeQuery(id+"F6.boolean.opBoolean","COPY",EDGE,{"derivedFrom":makeQuery(id+"F6.opExtrude","CAP_EDGE",EDGE,{"disambiguationData":[OSD([sQuery(id+"F5.wireOp",EDGE,"E82")])],"isStart":false})}),"instanceName":"1"});
            fillet(context, id + "F24", {"entities" : qUnion([Q0, Q1, Q2, Q3, Q4, Q5, Q6, Q7, Q8, Q9, Q10, Q11, Q12, Q13, Q14, Q15]), "radius" : 1 * mm, "tangentPropagation" : true, "allowEdgeOverflow" : false});
        }
        {
            var Q0;
            Q0=makeQuery(id+"F21.boolean.opBoolean","INTERSECT",EDGE,{"derivedFrom":[makeQuery(id+"F8.boolean.opBoolean","COPY",FACE,{"derivedFrom":makeQuery(id+"F8.opExtrude","SWEPT_FACE",FACE,{"disambiguationData":[OSD([sQuery(id+"F7.wireOp",EDGE,"E87")])]})}),makeQuery(id+"F21.opRevolve","SWEPT_FACE",FACE,{"disambiguationData":[OSD([sQuery(id+"F20.wireOp",EDGE,"E116")])]})]});
            var Q1;
            Q1=makeQuery(id+"F21.boolean.opBoolean","INTERSECT",EDGE,{"derivedFrom":[makeQuery(id+"F19.opPattern","COPY",FACE,{"derivedFrom":makeQuery(id+"F8.boolean.opBoolean","COPY",FACE,{"derivedFrom":makeQuery(id+"F8.opExtrude","SWEPT_FACE",FACE,{"disambiguationData":[OSD([sQuery(id+"F7.wireOp",EDGE,"E87")])]})}),"instanceName":"1"}),makeQuery(id+"F21.opRevolve","SWEPT_FACE",FACE,{"disambiguationData":[OSD([sQuery(id+"F20.wireOp",EDGE,"E116")])]})]});
            var Q2;
            Q2=makeQuery(id+"F21.boolean.opBoolean","INTERSECT",EDGE,{"derivedFrom":[makeQuery(id+"F19.opPattern","COPY",FACE,{"derivedFrom":makeQuery(id+"F8.boolean.opBoolean","COPY",FACE,{"derivedFrom":makeQuery(id+"F8.opExtrude","SWEPT_FACE",FACE,{"disambiguationData":[OSD([sQuery(id+"F7.wireOp",EDGE,"E87")])]})}),"instanceName":"2"}),makeQuery(id+"F21.opRevolve","SWEPT_FACE",FACE,{"disambiguationData":[OSD([sQuery(id+"F20.wireOp",EDGE,"E116")])]})]});
            var Q3;
            Q3=makeQuery(id+"F21.boolean.opBoolean","INTERSECT",EDGE,{"derivedFrom":[makeQuery(id+"F19.boolean.opBoolean","MERGE",FACE,{"disambiguationData":[OD(1.0)],"derivedFrom":[makeQuery(id+"F19.opPattern","COPY",FACE,{"derivedFrom":makeQuery(id+"F8.boolean.opBoolean","COPY",FACE,{"derivedFrom":makeQuery(id+"F8.opExtrude","SWEPT_FACE",FACE,{"disambiguationData":[OSD([sQuery(id+"F7.wireOp",EDGE,"E94.MirrorCS")])]})}),"instanceName":"1"}),makeQuery(id+"F19.opPattern","COPY",FACE,{"derivedFrom":makeQuery(id+"F8.boolean.opBoolean","COPY",FACE,{"derivedFrom":makeQuery(id+"F8.opExtrude","SWEPT_FACE",FACE,{"disambiguationData":[OSD([sQuery(id+"F7.wireOp",EDGE,"E87")])]})}),"instanceName":"3"})]}),makeQuery(id+"F21.opRevolve","SWEPT_FACE",FACE,{"disambiguationData":[OSD([sQuery(id+"F20.wireOp",EDGE,"E116")])]})]});
            fillet(context, id + "F25", {"entities" : qUnion([Q0, Q1, Q2, Q3]), "radius" : 6 * mm, "tangentPropagation" : true, "allowEdgeOverflow" : false});
        }
        {
            var Q0;
            Q0=makeQuery(id+"F8.boolean.opBoolean","COPY",EDGE,{"derivedFrom":makeQuery(id+"F8.opExtrude","SWEPT_EDGE",EDGE,{"disambiguationData":[OSD([sQuery(id+"F7.wireOp",EDGE,"E87"),sQuery(id+"F7.wireOp",EDGE,"E96")])]})});
            var Q1;
            Q1=makeQuery(id+"F19.opPattern","COPY",EDGE,{"derivedFrom":makeQuery(id+"F8.boolean.opBoolean","COPY",EDGE,{"derivedFrom":makeQuery(id+"F8.opExtrude","SWEPT_EDGE",EDGE,{"disambiguationData":[OSD([sQuery(id+"F7.wireOp",EDGE,"E87"),sQuery(id+"F7.wireOp",EDGE,"E96")])]})}),"instanceName":"1"});
            var Q2;
            Q2=makeQuery(id+"F19.opPattern","COPY",EDGE,{"derivedFrom":makeQuery(id+"F8.boolean.opBoolean","COPY",EDGE,{"derivedFrom":makeQuery(id+"F8.opExtrude","SWEPT_EDGE",EDGE,{"disambiguationData":[OSD([sQuery(id+"F7.wireOp",EDGE,"E87"),sQuery(id+"F7.wireOp",EDGE,"E96")])]})}),"instanceName":"2"});
            var Q3;
            {var subQ0=sQuery(id+"F7.wireOp",EDGE,"E96");var subQ1=sQuery(id+"F7.wireOp",EDGE,"E94.MirrorCS");var subQ2=sQuery(id+"F7.wireOp",EDGE,"E97");var subQ3=makeQuery(id+"F8.boolean.opBoolean","COPY",FACE,{"derivedFrom":makeQuery(id+"F8.opExtrude","SWEPT_FACE",FACE,{"disambiguationData":[OSD([subQ2])]})});var subQ4=sQuery(id+"F7.wireOp",EDGE,"E87");Q3=makeQuery(id+"F19.boolean.opBoolean","MERGE",EDGE,{"disambiguationData":[topologyDisambiguationEdgeConnected([subQ3])],"derivedFrom":[makeQuery(id+"F19.opPattern","COPY",EDGE,{"derivedFrom":makeQuery(id+"F8.boolean.opBoolean","COPY",EDGE,{"derivedFrom":makeQuery(id+"F8.opExtrude","SWEPT_EDGE",EDGE,{"disambiguationData":[OSD([subQ1,subQ2])]})}),"instanceName":"1"}),makeQuery(id+"F19.opPattern","COPY",EDGE,{"derivedFrom":makeQuery(id+"F8.boolean.opBoolean","COPY",EDGE,{"derivedFrom":makeQuery(id+"F8.opExtrude","SWEPT_EDGE",EDGE,{"disambiguationData":[OSD([subQ4,subQ0])]})}),"instanceName":"3"})]});}
            fillet(context, id + "F26", {"entities" : qUnion([Q0, Q1, Q2, Q3]), "radius" : 3 * mm, "tangentPropagation" : true, "allowEdgeOverflow" : false});
        }
        {
            var Q0;
            Q0=qCreatedBy(id+"F1.planeOp",FACE);
            var sketch = newSketch(context, id + "F27", { "sketchPlane" : qUnion([Q0])});
            skLineSegment(sketch, "E121.0", {"start": v(55.2, 30) * mm, "end": v(55.2, -2.97) * mm});
            skLineSegment(sketch, "E122.0", {"start": v(50.53, -10) * mm, "end": v(36.77, -61.35) * mm});
            skArc(sketch, "E123.0", {"start": v(31.75, -65.2) * mm, "mid": v(34.92, -64.13) * mm, "end": v(36.77, -61.35) * mm});
            skLineSegment(sketch, "E124.0", {"start": v(31.75, -65.2) * mm, "end": v(0, -65.2) * mm});
            skLineSegment(sketch, "E125", {"start": v(0, -65.2) * mm, "end": v(0, 30) * mm});
            skLineSegment(sketch, "E126", {"start": v(0, 30) * mm, "end": v(55.2, 30) * mm});
            skArc(sketch, "E127", {"start": v(53.25, -6.4) * mm, "mid": v(51.54, -7.94) * mm, "end": v(50.53, -10) * mm});
            skPoint(sketch, "E128.visualSharp", {"position": v(55.2, -5.66) * mm});
            skArc(sketch, "E128.filletArc", {"start": v(53.25, -6.4) * mm, "mid": v(54.68, -4.94) * mm, "end": v(55.2, -2.97) * mm});
            skSolve(sketch);
        }
        {
            var Q0;
            Q0 = qSketchRegion(id + "F27", true);
            var Q1;
            Q1=sQuery(id+"F2.wireOp",EDGE,"E9");
            revolve(context, id + "F28", {"operationType" : NewBodyOperationType.REMOVE, "surfaceOperationType" : NewSurfaceOperationType.NEW, "entities" : qUnion([Q0]), "axis" : qUnion([Q1]), "revolveType" : RevolveType.FULL, "oppositeDirection" : true});
        }
        {
            var Q0;
            Q0=qCreatedBy(makeId("Front.planeOp"),FACE);
            var sketch = newSketch(context, id + "F29", { "sketchPlane" : qUnion([Q0])});
            skCircle(sketch, "E129", {"center": v(25, -26) * mm, "radius": 11 * mm});
            skSolve(sketch);
        }
        {
            var Q0;
            Q0 = qSketchRegion(id + "F29", true);
            extrude(context, id + "F30", {"entities" : qUnion([Q0]), "operationType" : NewBodyOperationType.ADD, "endBound" : BoundingType.SYMMETRIC, "depth" : 130 * mm, "offsetDistance" : 25 * mm});
        }
    });
